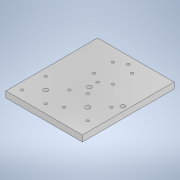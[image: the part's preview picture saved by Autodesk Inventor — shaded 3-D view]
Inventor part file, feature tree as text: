
AUTODESK INVENTOR PART (.ipt)
format: ipt  version: 2022.2 (Build 262287010, 287A)  size: 168,960 bytes
history: native  units: mm
features: sketch x6, hole x5, extrude x3
ambient origin geometry x8: Origin, YZ Plane, XZ Plane, XY Plane, X Axis, Y Axis, Z Axis, Center Point
bodies: Volumenkörper1 (feature_tree)
feature tree (14):
  extrude  "Extrusion1"  Depth=120.0mm
  hole  "Rail_through_holes"  [1 undecoded]
  hole  "Slide_through_holes"  [1 undecoded]
  sketch  "Skizze4"  dims[d6=3.4mm d7=8.0mm d8=4.0mm d9=2.0mm d10=90.0deg d11=8.8mm d12=20.594885mm d13=25.0mm]
  hole  "Nema_X_through_holes"  [1 undecoded]
  extrude  "Nema_X_Shaft"  Depth=8.0mm
  sketch  "Skizze5"  dims[d14=25.0mm d15=20.0mm]
  hole  "Nema_Y_through_holes"  [1 undecoded]
  extrude  "Nema_Y_Shaft"  Depth=8.0mm
  hole  "Y_Pulley_Shafts"  [1 undecoded]
  sketch  "Skizze1"  dims[d0=100.0mm d1=120.0mm]
  sketch  "Skizze2"  dims[d2=8.0mm d3=0.0mm d4=40.0mm]
  sketch  "Skizze3"  dims[d5=10.0mm]
  sketch  "Skizze6"  dims[d16=3.4mm d17=8.0mm d18=6.5mm d19=3.4mm d20=90.0deg d21=8.0mm d22=20.594885mm d23=25.0mm d24=31.0mm d25=31.0mm d26=93.0mm d27=3.4mm d28=6.0mm d29=4.0mm d30=2.0mm d31=90.0deg d32=8.0mm d33=20.594885mm d34=22.0mm d35=31.0mm d36=31.0mm d37=3.4mm d38=6.0mm d39=4.0mm d40=2.0mm d41=90.0deg d42=8.0mm d43=20.594885mm d45=0.0mm d46=0.0mm d47=85.0mm d48=35.0mm d49=30.0mm d50=44.0mm d51=24.0mm d52=5.5mm d53=6.0mm d54=10.0mm d55=5.7mm d56=90.0deg d57=8.0mm d58=20.594885mm d59=6.0mm d60=6.0mm d61=0.0mm d62=0.0mm]
note: 5 required parameter values undecoded (feature->parameter linkage not recoverable at this tier; creation-order binding heuristic only, values carry confidence <= 0.55)
